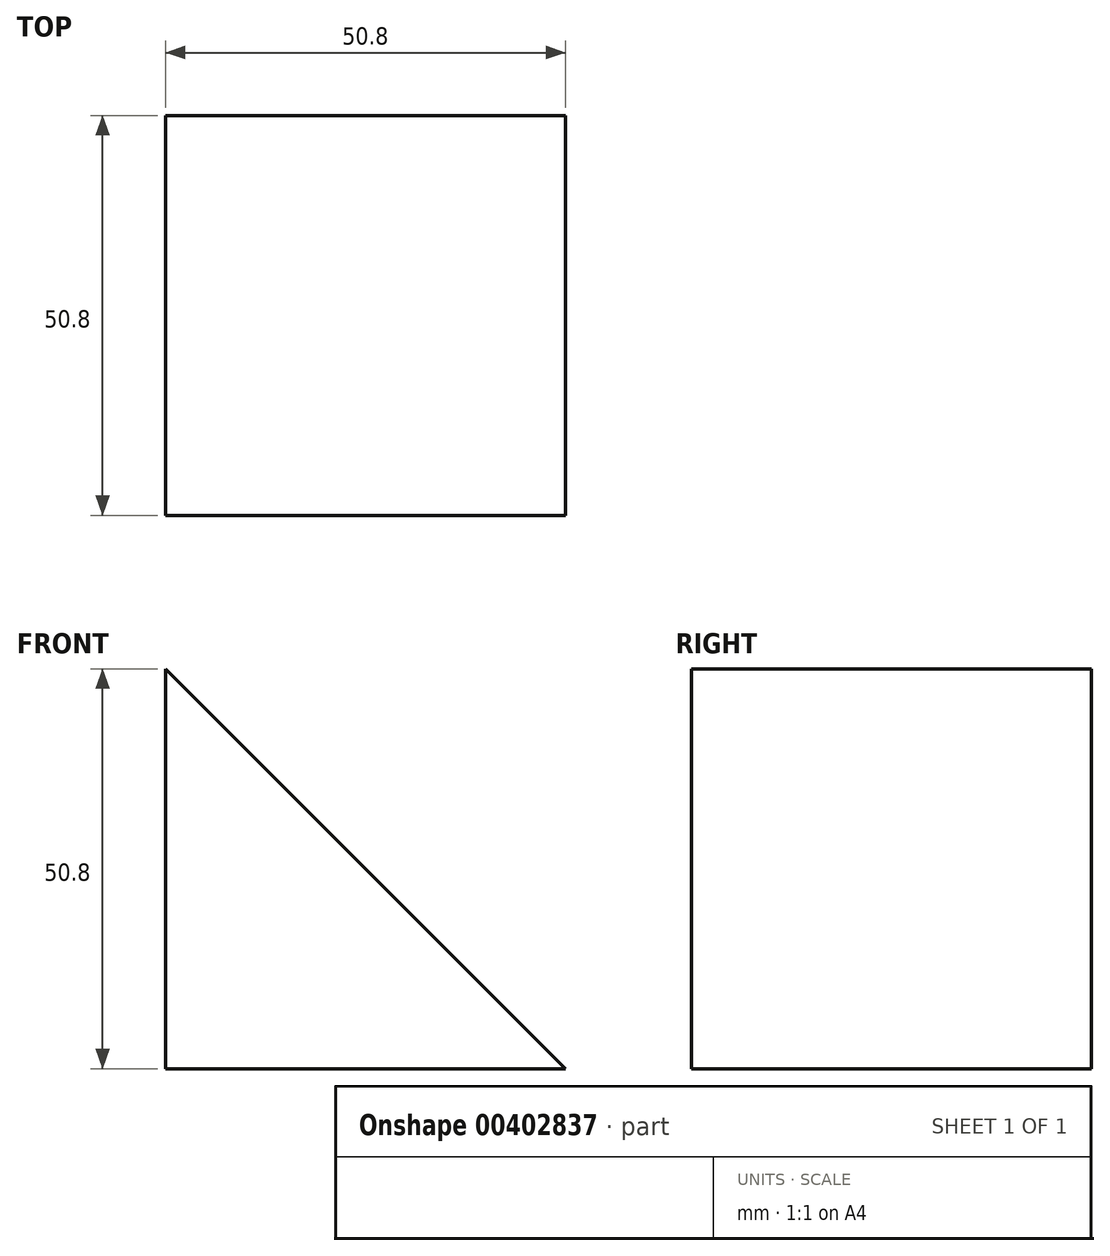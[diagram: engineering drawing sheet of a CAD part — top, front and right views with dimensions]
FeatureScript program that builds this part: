
annotation { "Feature Type Name" : "Feature", "Feature Type Description" : "" }
export const myFeature = defineFeature(function(context is Context, id is Id, definition is map)
    precondition{}
    {
        {
            var Q0;
            Q0=qCreatedBy(makeId("Front.planeOp"),FACE);
            var sketch = newSketch(context, id + "F0", { "sketchPlane" : qUnion([Q0])});
            skLineSegment(sketch, "E0", {"start": v(0, 0) * mm, "end": v(0, 50.8) * mm});
            skLineSegment(sketch, "E1", {"start": v(0, 0) * mm, "end": v(50.8, 0) * mm});
            skLineSegment(sketch, "E2", {"start": v(0, 50.8) * mm, "end": v(50.8, 0) * mm});
            skSolve(sketch);
        }
        {
            var Q0;
            Q0 = qSketchRegion(id + "F0", true);
            extrude(context, id + "F1", {"entities" : qUnion([Q0]), "depth" : 50.8 * mm});
        }
    });
